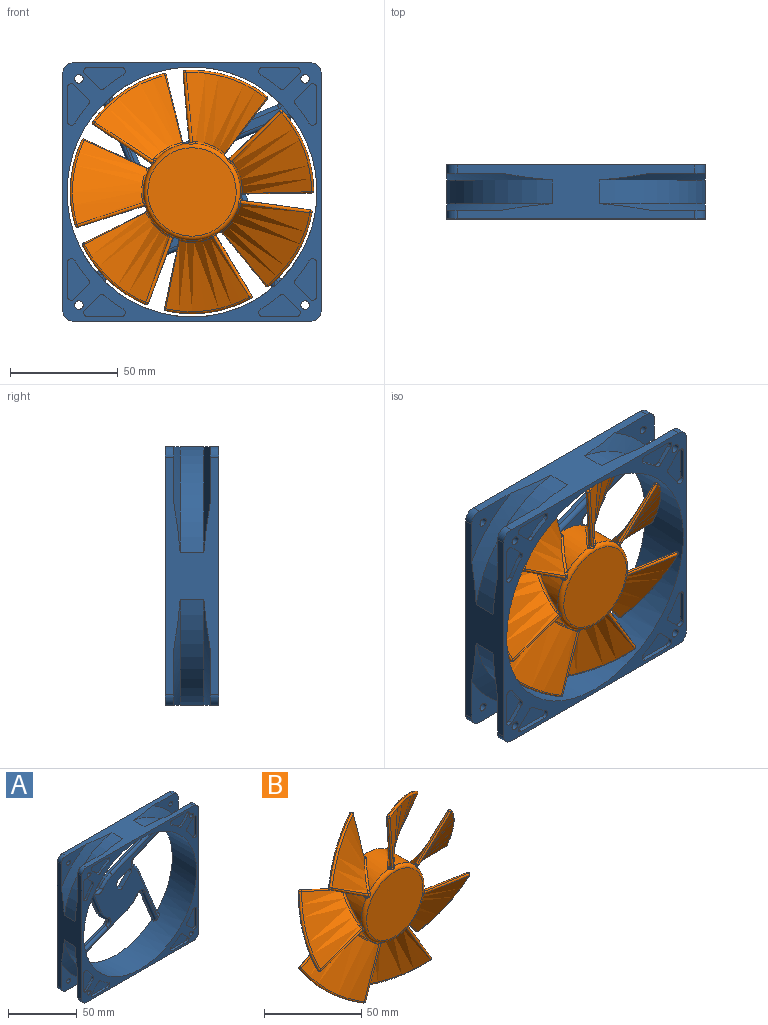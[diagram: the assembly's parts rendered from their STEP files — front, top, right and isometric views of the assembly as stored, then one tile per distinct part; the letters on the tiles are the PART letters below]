
ASSEMBLY  parts=2 mates=1
PART A: 223 faces, bbox 135.7x25x135.7 mm
  f0: plane 88.49x86.45mm, normal (0,-1,0), area 1656.3mm2, adj f15,f184,f185,f186,f187,f196,f197,f198
  f1: plane 120x120mm, normal (0,1,0), area 4802mm2, adj f2,f3,f5,f11,f12,f13,f14,f15
  f2: plane 110x25mm, normal (1,0,0), area 1352.3mm2, adj f1,f6,f23,f24,f25,f26,f27,f28
  f3: plane 6.72x2mm, normal (-1,0,0), area 13.4mm2, adj f1,f4,f35,f192
  f4: plane 65.36x42.4mm, normal (0,1,0), area 561.7mm2, adj f3,f5,f32,f33,f34,f35,f36,f182
  f5: cylinder r=2mm len=2mm, axis (0,1,0), area 1.5mm2, adj f1,f4,f32,f183
  f6: plane 120x120mm, normal (0,-1,0), area 2727.1mm2, adj f2,f7,f8,f9,f10,f12,f13,f14
  f7: cylinder r=2mm len=4mm, axis (0,1,0), area 50.3mm2, adj f6,f31
  f8: cylinder r=2mm len=4mm, axis (0,1,0), area 50.3mm2, adj f6,f26
  f9: cylinder r=2mm len=4mm, axis (0,1,0), area 50.3mm2, adj f6,f24
  f10: cylinder r=2mm len=4mm, axis (0,1,0), area 50.3mm2, adj f6,f21
  f11: plane 11.44x4mm, normal (1,0,0), area 45.8mm2, adj f1,f27,f142,f193
  f12: plane 110x25mm, normal (0,0,1), area 1413.4mm2, adj f1,f6,f26,f27,f28,f29,f30,f31
  f13: plane 110x25mm, normal (-1,0,0), area 1413.4mm2, adj f1,f6,f20,f21,f22,f29,f30,f31
  f14: plane 110x25mm, normal (0,0,-1), area 1413.4mm2, adj f1,f6,f20,f21,f22,f23,f24,f25
  f15: cylinder r=58mm len=116mm, axis (0,1,0), area 8990.7mm2, adj f0,f1,f6,f174,f175,f176,f177,f178
  f16: cylinder r=2mm len=4mm, axis (0,1,0), area 50.3mm2, adj f1,f30
  f17: cylinder r=2mm len=4mm, axis (0,1,0), area 50.3mm2, adj f1,f27
  f18: cylinder r=2mm len=4mm, axis (0,1,0), area 50.3mm2, adj f1,f23
  f19: cylinder r=2mm len=4mm, axis (0,1,0), area 50.3mm2, adj f1,f20
  f20: plane 25.93x25.93mm, normal (0,-1,0), area 257.3mm2, adj f13,f14,f19,f144,f151
  f21: plane 25.93x25.93mm, normal (0,1,0), area 257.3mm2, adj f10,f13,f14,f148,f154
  f22: cylinder r=61mm len=49mm, axis (0,1,0), area 810.7mm2, adj f13,f14,f151,f154
  f23: plane 25.93x25.93mm, normal (0,-1,0), area 257.3mm2, adj f2,f14,f18,f145,f152
  f24: plane 25.93x25.93mm, normal (0,1,0), area 257.3mm2, adj f2,f9,f14,f149,f155
  f25: cylinder r=61mm len=49mm, axis (0,1,0), area 810.7mm2, adj f2,f14,f152,f155
  f26: plane 25.93x25.93mm, normal (0,1,0), area 257.3mm2, adj f2,f8,f12,f146,f156
  f27: plane 25.93x25.93mm, normal (0,-1,0), area 240.5mm2, adj f2,f11,f12,f17,f142,f153,f191,f192
  f28: cylinder r=61mm len=49mm, axis (0,1,0), area 810.7mm2, adj f2,f12,f153,f156
  f29: cylinder r=61mm len=49mm, axis (0,1,0), area 810.7mm2, adj f12,f13,f150,f157
  f30: plane 25.93x25.93mm, normal (0,-1,0), area 257.3mm2, adj f12,f13,f16,f143,f150
  f31: plane 25.93x25.93mm, normal (0,1,0), area 257.3mm2, adj f7,f12,f13,f147,f157
  f32: plane 6.31x6.31mm, normal (0.71,0,-0.71), area 17.9mm2, adj f1,f4,f5,f36
  f33: cylinder r=63mm len=5.42mm, axis (0,1,0), area 13mm2, adj f1,f4,f35,f182
  f34: plane 4.66x2mm, normal (-1,0,0), area 9.3mm2, adj f1,f4,f36,f193
  f35: cylinder r=2mm len=3.72mm, axis (0,1,0), area 10.4mm2, adj f1,f3,f4,f33
  f36: cylinder r=2mm len=3.41mm, axis (0,-1,0), area 9.4mm2, adj f1,f4,f32,f34
  f37: plane 6.31x6.31mm, normal (-0.71,0,0.71), area 17.9mm2, adj f1,f40,f41,f43
  f38: plane 15.22x2mm, normal (0,0,-1), area 30.4mm2, adj f1,f40,f42,f43
  f39: cylinder r=63mm len=8.63mm, axis (0,1,0), area 21.2mm2, adj f1,f40,f41,f42
  f40: plane 19.22x10.31mm, normal (0,1,0), area 129.1mm2, adj f37,f38,f39,f41,f42,f43
  f41: cylinder r=2mm len=2.7mm, axis (0,1,0), area 5.9mm2, adj f1,f37,f39,f40
  f42: cylinder r=2mm len=3.72mm, axis (0,1,0), area 10.4mm2, adj f1,f38,f39,f40
  f43: cylinder r=2mm len=3.41mm, axis (0,-1,0), area 9.4mm2, adj f1,f37,f38,f40
  f44: plane 6.31x6.31mm, normal (-0.71,0,-0.71), area 17.9mm2, adj f1,f47,f48,f50
  f45: cylinder r=63mm len=8.63mm, axis (0,1,0), area 21.2mm2, adj f1,f47,f48,f49
  f46: plane 15.22x2mm, normal (0,0,1), area 30.4mm2, adj f1,f47,f49,f50
  f47: plane 19.22x10.31mm, normal (0,1,0), area 129.1mm2, adj f44,f45,f46,f48,f49,f50
  f48: cylinder r=2mm len=2.7mm, axis (0,1,0), area 5.9mm2, adj f1,f44,f45,f47
  f49: cylinder r=2mm len=3.72mm, axis (0,1,0), area 10.4mm2, adj f1,f45,f46,f47
  f50: cylinder r=2mm len=3.41mm, axis (0,-1,0), area 9.4mm2, adj f1,f44,f46,f47
  f51: plane 6.31x6.31mm, normal (-0.71,0,-0.71), area 17.9mm2, adj f1,f54,f55,f57
  f52: plane 15.22x2mm, normal (1,0,0), area 30.4mm2, adj f1,f54,f56,f57
  f53: cylinder r=63mm len=8.63mm, axis (0,1,0), area 21.2mm2, adj f1,f54,f55,f56
  f54: plane 19.22x10.31mm, normal (0,1,0), area 129.1mm2, adj f51,f52,f53,f55,f56,f57
  f55: cylinder r=2mm len=2.7mm, axis (0,1,0), area 5.9mm2, adj f1,f51,f53,f54
  f56: cylinder r=2mm len=3.72mm, axis (0,1,0), area 10.4mm2, adj f1,f52,f53,f54
  f57: cylinder r=2mm len=3.41mm, axis (0,-1,0), area 9.4mm2, adj f1,f51,f52,f54
  f58: plane 6.31x6.31mm, normal (-0.71,0,0.71), area 17.9mm2, adj f1,f61,f62,f64
  f59: cylinder r=63mm len=8.63mm, axis (0,1,0), area 21.2mm2, adj f1,f61,f62,f63
  f60: plane 15.22x2mm, normal (1,0,0), area 30.4mm2, adj f1,f61,f63,f64
  f61: plane 19.22x10.31mm, normal (0,1,0), area 129.1mm2, adj f58,f59,f60,f62,f63,f64
  f62: cylinder r=2mm len=2.7mm, axis (0,1,0), area 5.9mm2, adj f1,f58,f59,f61
  f63: cylinder r=2mm len=3.72mm, axis (0,1,0), area 10.4mm2, adj f1,f59,f60,f61
  f64: cylinder r=2mm len=3.41mm, axis (0,-1,0), area 9.4mm2, adj f1,f58,f60,f61
  f65: plane 6.31x6.31mm, normal (0.71,0,-0.71), area 17.9mm2, adj f1,f68,f69,f71
  f66: plane 15.22x2mm, normal (0,0,1), area 30.4mm2, adj f1,f68,f70,f71
  f67: cylinder r=63mm len=8.63mm, axis (0,1,0), area 21.2mm2, adj f1,f68,f69,f70
  f68: plane 19.22x10.31mm, normal (0,1,0), area 129.1mm2, adj f65,f66,f67,f69,f70,f71
  f69: cylinder r=2mm len=2.7mm, axis (0,1,0), area 5.9mm2, adj f1,f65,f67,f68
  f70: cylinder r=2mm len=3.72mm, axis (0,1,0), area 10.4mm2, adj f1,f66,f67,f68
  f71: cylinder r=2mm len=3.41mm, axis (0,-1,0), area 9.4mm2, adj f1,f65,f66,f68
  f72: plane 6.31x6.31mm, normal (0.71,0,0.71), area 17.9mm2, adj f1,f75,f76,f78
  f73: cylinder r=63mm len=8.63mm, axis (0,1,0), area 21.2mm2, adj f1,f75,f76,f77
  f74: plane 15.22x2mm, normal (0,0,-1), area 30.4mm2, adj f1,f75,f77,f78
  f75: plane 19.22x10.31mm, normal (0,1,0), area 129.1mm2, adj f72,f73,f74,f76,f77,f78
  f76: cylinder r=2mm len=2.7mm, axis (0,1,0), area 5.9mm2, adj f1,f72,f73,f75
  f77: cylinder r=2mm len=3.72mm, axis (0,1,0), area 10.4mm2, adj f1,f73,f74,f75
  f78: cylinder r=2mm len=3.41mm, axis (0,-1,0), area 9.4mm2, adj f1,f72,f74,f75
  f79: plane 6.31x6.31mm, normal (0.71,0,0.71), area 17.9mm2, adj f1,f82,f83,f85
  f80: plane 15.22x2mm, normal (-1,0,0), area 30.4mm2, adj f1,f82,f84,f85
  f81: cylinder r=63mm len=8.63mm, axis (0,1,0), area 21.2mm2, adj f1,f82,f83,f84
  f82: plane 19.22x10.31mm, normal (0,1,0), area 129.1mm2, adj f79,f80,f81,f83,f84,f85
  f83: cylinder r=2mm len=2.7mm, axis (0,1,0), area 5.9mm2, adj f1,f79,f81,f82
  f84: cylinder r=2mm len=3.72mm, axis (0,1,0), area 10.4mm2, adj f1,f80,f81,f82
  f85: cylinder r=2mm len=3.41mm, axis (0,-1,0), area 9.4mm2, adj f1,f79,f80,f82
  f86: plane 6.31x6.31mm, normal (0.71,0,-0.71), area 17.9mm2, adj f6,f89,f90,f92
  f87: plane 15.22x2mm, normal (-1,0,0), area 30.4mm2, adj f6,f89,f91,f92
  f88: cylinder r=63mm len=8.63mm, axis (0,-1,0), area 21.2mm2, adj f6,f89,f90,f91
  f89: plane 19.22x10.31mm, normal (0,-1,0), area 129.1mm2, adj f86,f87,f88,f90,f91,f92
  f90: cylinder r=2mm len=2.7mm, axis (0,-1,0), area 5.9mm2, adj f6,f86,f88,f89
  f91: cylinder r=2mm len=3.72mm, axis (0,-1,0), area 10.4mm2, adj f6,f87,f88,f89
  f92: cylinder r=2mm len=3.41mm, axis (0,1,0), area 9.4mm2, adj f6,f86,f87,f89
  f93: plane 6.31x6.31mm, normal (-0.71,0,0.71), area 17.9mm2, adj f6,f96,f97,f99
  f94: cylinder r=63mm len=8.63mm, axis (0,-1,0), area 21.2mm2, adj f6,f96,f97,f98
  f95: plane 15.22x2mm, normal (0,0,-1), area 30.4mm2, adj f6,f96,f98,f99
  f96: plane 19.22x10.31mm, normal (0,-1,0), area 129.1mm2, adj f93,f94,f95,f97,f98,f99
  f97: cylinder r=2mm len=2.7mm, axis (0,-1,0), area 5.9mm2, adj f6,f93,f94,f96
  f98: cylinder r=2mm len=3.72mm, axis (0,-1,0), area 10.4mm2, adj f6,f94,f95,f96
  f99: cylinder r=2mm len=3.41mm, axis (0,1,0), area 9.4mm2, adj f6,f93,f95,f96
  f100: plane 6.31x6.31mm, normal (-0.71,0,-0.71), area 17.9mm2, adj f6,f103,f104,f106
  f101: plane 15.22x2mm, normal (0,0,1), area 30.4mm2, adj f6,f103,f105,f106
  f102: cylinder r=63mm len=8.63mm, axis (0,-1,0), area 21.2mm2, adj f6,f103,f104,f105
  f103: plane 19.22x10.31mm, normal (0,-1,0), area 129.1mm2, adj f100,f101,f102,f104,f105,f106
  f104: cylinder r=2mm len=2.7mm, axis (0,-1,0), area 5.9mm2, adj f6,f100,f102,f103
  f105: cylinder r=2mm len=3.72mm, axis (0,-1,0), area 10.4mm2, adj f6,f101,f102,f103
  f106: cylinder r=2mm len=3.41mm, axis (0,1,0), area 9.4mm2, adj f6,f100,f101,f103
  f107: plane 6.31x6.31mm, normal (-0.71,0,-0.71), area 17.9mm2, adj f6,f110,f111,f113
  f108: cylinder r=63mm len=8.63mm, axis (0,-1,0), area 21.2mm2, adj f6,f110,f111,f112
  f109: plane 15.22x2mm, normal (1,0,0), area 30.4mm2, adj f6,f110,f112,f113
  f110: plane 19.22x10.31mm, normal (0,-1,0), area 129.1mm2, adj f107,f108,f109,f111,f112,f113
  f111: cylinder r=2mm len=2.7mm, axis (0,-1,0), area 5.9mm2, adj f6,f107,f108,f110
  f112: cylinder r=2mm len=3.72mm, axis (0,-1,0), area 10.4mm2, adj f6,f108,f109,f110
  f113: cylinder r=2mm len=3.41mm, axis (0,1,0), area 9.4mm2, adj f6,f107,f109,f110
  f114: plane 6.31x6.31mm, normal (-0.71,0,0.71), area 17.9mm2, adj f6,f117,f118,f120
  f115: plane 15.22x2mm, normal (1,0,0), area 30.4mm2, adj f6,f117,f119,f120
  f116: cylinder r=63mm len=8.63mm, axis (0,-1,0), area 21.2mm2, adj f6,f117,f118,f119
  f117: plane 19.22x10.31mm, normal (0,-1,0), area 129.1mm2, adj f114,f115,f116,f118,f119,f120
  f118: cylinder r=2mm len=2.7mm, axis (0,-1,0), area 5.9mm2, adj f6,f114,f116,f117
  f119: cylinder r=2mm len=3.72mm, axis (0,-1,0), area 10.4mm2, adj f6,f115,f116,f117
  f120: cylinder r=2mm len=3.41mm, axis (0,1,0), area 9.4mm2, adj f6,f114,f115,f117
  f121: plane 6.31x6.31mm, normal (0.71,0,-0.71), area 17.9mm2, adj f6,f124,f125,f127
  f122: cylinder r=63mm len=8.63mm, axis (0,-1,0), area 21.2mm2, adj f6,f124,f125,f126
  f123: plane 15.22x2mm, normal (0,0,1), area 30.4mm2, adj f6,f124,f126,f127
  f124: plane 19.22x10.31mm, normal (0,-1,0), area 129.1mm2, adj f121,f122,f123,f125,f126,f127
  f125: cylinder r=2mm len=2.7mm, axis (0,-1,0), area 5.9mm2, adj f6,f121,f122,f124
  f126: cylinder r=2mm len=3.72mm, axis (0,-1,0), area 10.4mm2, adj f6,f122,f123,f124
  f127: cylinder r=2mm len=3.41mm, axis (0,1,0), area 9.4mm2, adj f6,f121,f123,f124
  f128: plane 6.31x6.31mm, normal (0.71,0,0.71), area 17.9mm2, adj f6,f131,f132,f134
  f129: plane 15.22x2mm, normal (0,0,-1), area 30.4mm2, adj f6,f131,f133,f134
  f130: cylinder r=63mm len=8.63mm, axis (0,-1,0), area 21.2mm2, adj f6,f131,f132,f133
  f131: plane 19.22x10.31mm, normal (0,-1,0), area 129.1mm2, adj f128,f129,f130,f132,f133,f134
  f132: cylinder r=2mm len=2.7mm, axis (0,-1,0), area 5.9mm2, adj f6,f128,f130,f131
  f133: cylinder r=2mm len=3.72mm, axis (0,-1,0), area 10.4mm2, adj f6,f129,f130,f131
  f134: cylinder r=2mm len=3.41mm, axis (0,1,0), area 9.4mm2, adj f6,f128,f129,f131
  f135: plane 6.31x6.31mm, normal (0.71,0,0.71), area 17.9mm2, adj f6,f138,f139,f141
  f136: cylinder r=63mm len=8.63mm, axis (0,-1,0), area 21.2mm2, adj f6,f138,f139,f140
  f137: plane 15.22x2mm, normal (-1,0,0), area 30.4mm2, adj f6,f138,f140,f141
  f138: plane 19.22x10.31mm, normal (0,-1,0), area 129.1mm2, adj f135,f136,f137,f139,f140,f141
  f139: cylinder r=2mm len=2.7mm, axis (0,-1,0), area 5.9mm2, adj f6,f135,f136,f138
  f140: cylinder r=2mm len=3.72mm, axis (0,-1,0), area 10.4mm2, adj f6,f136,f137,f138
  f141: cylinder r=2mm len=3.41mm, axis (0,1,0), area 9.4mm2, adj f6,f135,f137,f138
  f142: cylinder r=5mm len=5mm, axis (0,-1,0), area 31.4mm2, adj f1,f11,f12,f27
  f143: cylinder r=5mm len=5mm, axis (0,1,0), area 31.4mm2, adj f1,f12,f13,f30
  f144: cylinder r=5mm len=5mm, axis (0,-1,0), area 31.4mm2, adj f1,f13,f14,f20
  f145: cylinder r=5mm len=5mm, axis (0,1,0), area 31.4mm2, adj f1,f2,f14,f23
  f146: cylinder r=5mm len=5mm, axis (0,-1,0), area 31.4mm2, adj f2,f6,f12,f26
  f147: cylinder r=5mm len=5mm, axis (0,1,0), area 31.4mm2, adj f6,f12,f13,f31
  f148: cylinder r=5mm len=5mm, axis (0,-1,0), area 31.4mm2, adj f6,f13,f14,f21
  f149: cylinder r=5mm len=5mm, axis (0,1,0), area 31.4mm2, adj f2,f6,f14,f24
  f150: cone r=69mm half-angle=69.4deg, axis (0,1,0), area 445.3mm2, adj f12,f13,f29,f30
  f151: cone r=69mm half-angle=69.4deg, axis (0,1,0), area 445.3mm2, adj f13,f14,f20,f22
  f152: cone r=69mm half-angle=69.4deg, axis (0,1,0), area 445.3mm2, adj f2,f14,f23,f25
  f153: cone r=69mm half-angle=69.4deg, axis (0,1,0), area 445.3mm2, adj f2,f12,f27,f28
  f154: cone r=61mm half-angle=69.4deg, axis (0,-1,0), area 445.3mm2, adj f13,f14,f21,f22
  f155: cone r=61mm half-angle=69.4deg, axis (0,-1,0), area 445.3mm2, adj f2,f14,f24,f25
  f156: cone r=61mm half-angle=69.4deg, axis (0,-1,0), area 445.3mm2, adj f2,f12,f26,f28
  f157: cone r=61mm half-angle=69.4deg, axis (0,-1,0), area 445.3mm2, adj f12,f13,f29,f31
  f158: plane 48.09x19.6mm, normal (-0.93,0,-0.38), area 103.9mm2, adj f1,f159,f174,f212
  f159: cylinder r=22.5mm len=10.34mm, axis (0,1,0), area 27.2mm2, adj f1,f158,f170,f213
  f160: plane 31.1x12.68mm, normal (-0.38,0,0.93), area 67.2mm2, adj f1,f170,f175,f215
  f161: plane 48.09x19.6mm, normal (0.38,0,-0.93), area 103.9mm2, adj f1,f162,f176,f218
  f162: cylinder r=22.5mm len=10.34mm, axis (0,1,0), area 27.2mm2, adj f1,f161,f171,f219
  f163: plane 31.1x12.68mm, normal (-0.93,0,-0.38), area 67.2mm2, adj f1,f171,f177,f221
  f164: plane 48.09x19.6mm, normal (0.93,0,0.38), area 103.9mm2, adj f1,f165,f178,f206
  f165: cylinder r=22.5mm len=8.48mm, axis (0,1,0), area 21.1mm2, adj f1,f164,f172,f207
  f166: plane 30.21x12.31mm, normal (0.38,0,-0.93), area 65.2mm2, adj f1,f172,f179,f209
  f167: plane 48.09x19.6mm, normal (-0.38,0,0.93), area 103.9mm2, adj f1,f168,f180,f200
  f168: cylinder r=22.5mm len=10.34mm, axis (0,1,0), area 27.2mm2, adj f1,f167,f173,f201
  f169: plane 31.1x12.68mm, normal (0.93,0,0.38), area 67.2mm2, adj f1,f173,f181,f203
  f170: cylinder r=3mm len=5.29mm, axis (0,1,0), area 13.1mm2, adj f1,f159,f160,f214
  f171: cylinder r=3mm len=5.29mm, axis (0,1,0), area 13.1mm2, adj f1,f162,f163,f220
  f172: cylinder r=3mm len=5.04mm, axis (0,1,0), area 12.2mm2, adj f1,f165,f166,f208
  f173: cylinder r=3mm len=5.29mm, axis (0,1,0), area 13.1mm2, adj f1,f168,f169,f202
  f174: cylinder r=1mm len=2mm, axis (0,1,0), area 4mm2, adj f1,f15,f158,f211
  f175: cylinder r=1mm len=2mm, axis (0,1,0), area 2.6mm2, adj f1,f15,f160,f216
  f176: cylinder r=1mm len=2mm, axis (0,1,0), area 4mm2, adj f1,f15,f161,f217
  f177: cylinder r=1mm len=2mm, axis (0,1,0), area 2.6mm2, adj f1,f15,f163,f222
  f178: cylinder r=1mm len=2mm, axis (0,1,0), area 4mm2, adj f1,f15,f164,f205
  f179: cylinder r=1mm len=2mm, axis (0,1,0), area 2.7mm2, adj f1,f15,f166,f210
  f180: cylinder r=1mm len=2mm, axis (0,1,0), area 4mm2, adj f1,f15,f167,f199
  f181: cylinder r=1mm len=2mm, axis (0,1,0), area 2.6mm2, adj f1,f15,f169,f204
  f182: plane 38.58x15.72mm, normal (-0.38,0,0.93), area 83.3mm2, adj f1,f4,f33,f189
  f183: plane 53.66x21.87mm, normal (0.38,0,-0.93), area 115.9mm2, adj f1,f4,f5,f190
  f184: plane 14.08x5.74mm, normal (0.93,0,0.38), area 39.7mm2, adj f0,f1,f4,f185,f190,f198
  f185: cylinder r=2.5mm len=4.09mm, axis (0,1,0), area 19.8mm2, adj f0,f1,f184,f186
  f186: plane 9.21x9.1mm, normal (-0.71,0,0.7), area 51.8mm2, adj f0,f1,f185,f187
  f187: cylinder r=2.5mm len=4mm, axis (0,1,0), area 11.2mm2, adj f0,f1,f4,f186,f188,f196
  f188: plane 3.81x2mm, normal (-0.93,0,-0.38), area 8.2mm2, adj f1,f4,f187,f189
  f189: cylinder r=2.5mm len=3.26mm, axis (0,1,0), area 7.9mm2, adj f1,f4,f182,f188
  f190: cylinder r=2.5mm len=3.26mm, axis (0,1,0), area 7.9mm2, adj f1,f4,f183,f184
  f191: cylinder r=0.5mm len=2mm, axis (0,1,0), area 1.1mm2, adj f4,f27,f192,f194
  f192: plane 4x3.21mm, normal (0,0,1), area 10.4mm2, adj f1,f2,f3,f4,f27,f191
  f193: plane 4.52x4mm, normal (0,0,-1), area 13mm2, adj f1,f4,f11,f27,f34,f195
  f194: plane 2.83x2mm, normal (0.91,0,0.42), area 6.2mm2, adj f4,f27,f191,f195
  f195: cylinder r=0.5mm len=2mm, axis (0,1,0), area 2mm2, adj f4,f27,f193,f194
  f196: cylinder r=2.5mm len=3.17mm, axis (0,1,0), area 7.4mm2, adj f0,f4,f187,f197
  f197: plane 11.02x4.49mm, normal (0.38,0,-0.93), area 23.8mm2, adj f0,f4,f196,f198
  f198: cylinder r=2.5mm len=3.26mm, axis (0,1,0), area 7.9mm2, adj f0,f4,f184,f197
  f199: torus R=3mm, axis (0,-1,0), area 5.8mm2, adj f0,f15,f180,f200
  f200: cylinder r=2mm len=48.84mm, axis (0.93,0,0.38), area 163.1mm2, adj f0,f167,f199,f201
  f201: torus R=20.5mm, axis (0,-1,0), area 41.4mm2, adj f0,f168,f200,f202
  f202: torus R=5mm, axis (0,-1,0), area 25.5mm2, adj f0,f173,f201,f203
  f203: cylinder r=2mm len=31.85mm, axis (0.38,0,-0.93), area 105.5mm2, adj f0,f169,f202,f204
  f204: torus R=3mm, axis (0,-1,0), area 1.9mm2, adj f0,f15,f181,f203
  f205: torus R=3mm, axis (0,-1,0), area 5.8mm2, adj f0,f15,f178,f206
  f206: cylinder r=2mm len=48.84mm, axis (0.38,0,-0.93), area 163.1mm2, adj f0,f164,f205,f207
  f207: torus R=20.5mm, axis (0,-1,0), area 32mm2, adj f0,f165,f206,f208
  f208: torus R=5mm, axis (0,-1,0), area 23.9mm2, adj f0,f172,f207,f209
  f209: cylinder r=2mm len=30.96mm, axis (-0.93,0,-0.38), area 102.5mm2, adj f0,f166,f208,f210
  f210: torus R=3mm, axis (0,-1,0), area 2.2mm2, adj f0,f15,f179,f209
  f211: torus R=3mm, axis (0,-1,0), area 5.8mm2, adj f0,f15,f174,f212
  f212: cylinder r=2mm len=48.84mm, axis (-0.38,0,0.93), area 163.1mm2, adj f0,f158,f211,f213
  f213: torus R=20.5mm, axis (0,-1,0), area 41.4mm2, adj f0,f159,f212,f214
  f214: torus R=5mm, axis (0,-1,0), area 25.5mm2, adj f0,f170,f213,f215
  f215: cylinder r=2mm len=31.85mm, axis (0.93,0,0.38), area 105.5mm2, adj f0,f160,f214,f216
  f216: torus R=3mm, axis (0,-1,0), area 1.9mm2, adj f0,f15,f175,f215
  f217: torus R=3mm, axis (0,-1,0), area 5.8mm2, adj f0,f15,f176,f218
  f218: cylinder r=2mm len=48.84mm, axis (-0.93,0,-0.38), area 163.1mm2, adj f0,f161,f217,f219
  f219: torus R=20.5mm, axis (0,-1,0), area 41.4mm2, adj f0,f162,f218,f220
  f220: torus R=5mm, axis (0,-1,0), area 25.5mm2, adj f0,f171,f219,f221
  f221: cylinder r=2mm len=31.85mm, axis (-0.38,0,0.93), area 105.5mm2, adj f0,f163,f220,f222
  f222: torus R=3mm, axis (0,-1,0), area 1.9mm2, adj f0,f15,f177,f221
PART B: 143 faces, bbox 115.5x27x115.7 mm
  f0: cylinder r=22.5mm len=28.95mm, axis (0,1,0), area 269.8mm2, adj f8,f72,f79,f81,f82,f133,f134
  f1: cylinder r=22.5mm len=25.02mm, axis (0,1,0), area 269.8mm2, adj f8,f72,f73,f74,f89,f91,f92
  f2: cylinder r=22.5mm len=27.37mm, axis (0,1,0), area 269.8mm2, adj f8,f72,f83,f84,f99,f101,f102
  f3: cylinder r=22.5mm len=27.74mm, axis (0,1,0), area 269.8mm2, adj f8,f72,f93,f94,f109,f111,f112
  f4: cylinder r=22.5mm len=24.42mm, axis (0,1,0), area 269.8mm2, adj f8,f72,f103,f104,f119,f121,f122
  f5: cylinder r=22.5mm len=29.07mm, axis (0,1,0), area 269.8mm2, adj f8,f72,f113,f114,f129,f131,f132
  f6: cylinder r=22.5mm len=21.04mm, axis (0,1,0), area 269.8mm2, adj f8,f72,f123,f124,f139,f141,f142
  f7: plane 41x41mm, normal (0,-1,0), area 1320.3mm2, adj f72
  f8: plane 45.12x45.12mm, normal (0,1,0), area 1590.4mm2, adj f0,f1,f2,f3,f4,f5,f6,f75
  f9: bspline ~48.93x45.75mm, area 1052.8mm2, adj f10,f12,f15,f141
  f10: bspline ~27.23x25.53mm, area 50.4mm2, adj f9,f11,f14,f140,f142
  f11: bspline ~24.34x23.49mm, area 50.8mm2, adj f10,f14,f138
  f12: bspline ~36.29x1.66mm, area 50.5mm2, adj f9,f13,f17,f137,f139
  f13: bspline ~36.94x1.66mm, area 50.4mm2, adj f12,f17,f133,f135
  f14: sphere r=1mm, area 3.8mm2, adj f10,f11,f15,f16
  f15: bspline ~39.27x19.01mm, area 69.1mm2, adj f9,f14,f16,f17
  f16: bspline ~39.38x19.01mm, area 69.1mm2, adj f14,f15,f17
  f17: sphere r=1mm, area 2.8mm2, adj f12,f13,f15,f16
  f18: bspline ~55.87x39.92mm, area 1052.8mm2, adj f19,f21,f24,f131
  f19: bspline ~36.44x3.68mm, area 50.4mm2, adj f18,f20,f23,f130,f132
  f20: bspline ~32.44x4.35mm, area 50.8mm2, adj f19,f23,f128
  f21: bspline ~29.36x23.45mm, area 50.5mm2, adj f18,f22,f26,f127,f129
  f22: bspline ~29.89x23.03mm, area 50.4mm2, adj f21,f26,f123,f125
  f23: sphere r=1mm, area 3.8mm2, adj f19,f20,f24,f25
  f24: bspline ~40.3x19.01mm, area 69.1mm2, adj f18,f23,f25,f26
  f25: bspline ~40.22x19.01mm, area 69.1mm2, adj f23,f24,f26
  f26: sphere r=1mm, area 2.8mm2, adj f21,f22,f24,f25
  f27: bspline ~49.21x48.75mm, area 1052.8mm2, adj f28,f30,f33,f121
  f28: bspline ~30.69x21.14mm, area 50.4mm2, adj f27,f29,f32,f120,f122
  f29: bspline ~27.9x18.94mm, area 50.8mm2, adj f28,f32,f118
  f30: bspline ~35.62x9.68mm, area 50.5mm2, adj f27,f31,f35,f117,f119
  f31: bspline ~36.01x9.83mm, area 50.4mm2, adj f30,f35,f113,f115
  f32: sphere r=1mm, area 3.8mm2, adj f28,f29,f33,f34
  f33: bspline ~34.86x24.31mm, area 69.1mm2, adj f27,f32,f34,f35
  f34: bspline ~35.24x23.75mm, area 69.1mm2, adj f32,f33,f35
  f35: sphere r=1mm, area 2.8mm2, adj f30,f31,f33,f34
  f36: bspline ~56.34x39.45mm, area 1052.8mm2, adj f37,f39,f42,f111
  f37: bspline ~35.08x11.67mm, area 50.4mm2, adj f36,f38,f41,f110,f112
  f38: bspline ~31.26x11.41mm, area 50.8mm2, adj f37,f41,f108
  f39: bspline ~33.37x16.7mm, area 50.5mm2, adj f36,f40,f44,f107,f109
  f40: bspline ~33.97x16.03mm, area 50.4mm2, adj f39,f44,f103,f105
  f41: sphere r=1mm, area 3.8mm2, adj f37,f38,f42,f43
  f42: bspline ~42.06x19.01mm, area 69.1mm2, adj f36,f41,f43,f44
  f43: bspline ~39.86x18.13mm, area 69.1mm2, adj f41,f42,f44
  f44: sphere r=1mm, area 2.8mm2, adj f39,f40,f42,f43
  f45: bspline ~49.3x47.01mm, area 1052.8mm2, adj f46,f48,f51,f101
  f46: bspline ~34.32x13.99mm, area 50.4mm2, adj f45,f47,f50,f100,f102
  f47: bspline ~30.91x12.6mm, area 50.8mm2, adj f46,f50,f98
  f48: bspline ~33.16x17.22mm, area 50.5mm2, adj f45,f49,f53,f97,f99
  f49: bspline ~33.28x17.51mm, area 50.4mm2, adj f48,f53,f93,f95
  f50: sphere r=1mm, area 3.8mm2, adj f46,f47,f51,f52
  f51: bspline ~31.27x28.78mm, area 69.1mm2, adj f45,f50,f52,f53
  f52: bspline ~30.72x29.34mm, area 69.1mm2, adj f50,f51,f53
  f53: sphere r=1mm, area 2.8mm2, adj f48,f49,f51,f52
  f54: bspline ~53.99x42.68mm, area 1052.8mm2, adj f55,f57,f60,f91
  f55: bspline ~31.95x19.08mm, area 50.4mm2, adj f54,f56,f59,f90,f92
  f56: bspline ~28.51x17.9mm, area 50.8mm2, adj f55,f59,f88
  f57: bspline ~35.69x9.11mm, area 50.5mm2, adj f54,f58,f62,f87,f89
  f58: bspline ~36.35x8.23mm, area 50.4mm2, adj f57,f62,f83,f85
  f59: sphere r=1mm, area 3.8mm2, adj f55,f56,f60,f61
  f60: bspline ~41.72x19.01mm, area 69.1mm2, adj f54,f59,f61,f62
  f61: bspline ~39.66x18.13mm, area 69.1mm2, adj f59,f60,f62
  f62: sphere r=1mm, area 2.8mm2, adj f57,f58,f60,f61
  f63: bspline ~52.59x43.95mm, area 1052.8mm2, adj f64,f66,f69,f81
  f64: bspline ~36.23x6.14mm, area 50.4mm2, adj f63,f65,f68,f80,f82
  f65: bspline ~32.38x5.62mm, area 50.8mm2, adj f64,f68,f78
  f66: bspline ~29.03x23.89mm, area 50.5mm2, adj f63,f67,f71,f77,f79
  f67: bspline ~28.88x24.31mm, area 50.4mm2, adj f66,f71,f73,f75
  f68: sphere r=1mm, area 3.8mm2, adj f64,f65,f69,f70
  f69: bspline ~36.67x21.42mm, area 69.1mm2, adj f63,f68,f70,f71
  f70: bspline ~36.38x21.97mm, area 69.1mm2, adj f68,f69,f71
  f71: sphere r=1mm, area 2.8mm2, adj f66,f67,f69,f70
  f72: torus R=20.5mm, axis (0,-1,0), area 399.1mm2, adj f0,f1,f2,f3,f4,f5,f6,f7
  f73: bspline ~3.19x1.73mm, area 3.2mm2, adj f1,f67,f74,f75
  f74: bspline ~18.77x14.22mm, area 31.6mm2, adj f1,f73,f76
  f75: bspline ~1.25x0.84mm, area 0mm2, adj f8,f67,f73,f77
  f76: bspline ~2.92x2.67mm, area 2.3mm2, adj f72,f74,f78
  f77: bspline ~2.41x2.19mm, area 2.1mm2, adj f8,f66,f75,f79
  f78: bspline ~3.17x1.53mm, area 2.2mm2, adj f65,f72,f76,f80
  f79: bspline ~1.5x1.16mm, area 0mm2, adj f0,f66,f77,f81
  f80: bspline ~1.52x1.39mm, area 1.2mm2, adj f64,f72,f78,f82
  f81: bspline ~23.03x19.48mm, area 35.5mm2, adj f0,f63,f79,f82
  f82: bspline ~2.15x1.56mm, area 1.7mm2, adj f0,f64,f80,f81
  f83: bspline ~3.19x1.35mm, area 3.2mm2, adj f2,f58,f84,f85
  f84: bspline ~18.77x17.65mm, area 31.6mm2, adj f2,f83,f86
  f85: bspline ~1.13x0.73mm, area 0mm2, adj f8,f58,f83,f87
  f86: bspline ~3.03x2.67mm, area 2.3mm2, adj f72,f84,f88
  f87: bspline ~2.64x1.45mm, area 2.1mm2, adj f8,f57,f85,f89
  f88: bspline ~2.88x1.93mm, area 2.2mm2, adj f56,f72,f86,f90
  f89: bspline ~1.3x1.16mm, area 0mm2, adj f1,f57,f87,f91
  f90: bspline ~1.39x1.36mm, area 1.2mm2, adj f55,f72,f88,f92
  f91: bspline ~21.59x19.42mm, area 35.5mm2, adj f1,f54,f89,f92
  f92: bspline ~2.15x1.57mm, area 1.7mm2, adj f1,f55,f90,f91
  f93: bspline ~3.19x1.7mm, area 3.2mm2, adj f3,f49,f94,f95
  f94: bspline ~18.77x14.05mm, area 31.6mm2, adj f3,f93,f96
  f95: bspline ~1.16x0.96mm, area 0mm2, adj f8,f49,f93,f97
  f96: bspline ~2.67x2.6mm, area 2.3mm2, adj f72,f94,f98
  f97: bspline ~2.71x1.87mm, area 2.1mm2, adj f8,f48,f95,f99
  f98: bspline ~2.95x1.93mm, area 2.2mm2, adj f47,f72,f96,f100
  f99: bspline ~1.42x1.16mm, area 0mm2, adj f2,f48,f97,f101
  f100: bspline ~1.55x1.39mm, area 1.2mm2, adj f46,f72,f98,f102
  f101: bspline ~23.03x17.03mm, area 35.5mm2, adj f2,f45,f99,f102
  f102: bspline ~1.95x1.57mm, area 1.7mm2, adj f2,f46,f100,f101
  f103: bspline ~3.19x1.54mm, area 3.2mm2, adj f4,f40,f104,f105
  f104: bspline ~18.77x17.12mm, area 31.6mm2, adj f4,f103,f106
  f105: bspline ~1.23x0.75mm, area 0mm2, adj f8,f40,f103,f107
  f106: bspline ~3.15x2.67mm, area 2.3mm2, adj f72,f104,f108
  f107: bspline ~2.71x1.89mm, area 2.1mm2, adj f8,f39,f105,f109
  f108: bspline ~3.14x1.5mm, area 2.2mm2, adj f38,f72,f106,f110
  f109: bspline ~1.44x1.16mm, area 0mm2, adj f3,f39,f107,f111
  f110: bspline ~1.39x1.29mm, area 1.2mm2, adj f37,f72,f108,f112
  f111: bspline ~23.03x21.38mm, area 35.5mm2, adj f3,f36,f109,f112
  f112: bspline ~2.15x1.37mm, area 1.7mm2, adj f3,f37,f110,f111
  f113: bspline ~3.19x1.58mm, area 3.2mm2, adj f5,f31,f114,f115
  f114: bspline ~18.77x16.07mm, area 31.6mm2, adj f5,f113,f116
  f115: bspline ~1.01x0.99mm, area 0mm2, adj f8,f31,f113,f117
  f116: bspline ~2.67x2.41mm, area 2.3mm2, adj f72,f114,f118
  f117: bspline ~2.94x1.46mm, area 2.1mm2, adj f8,f30,f115,f119
  f118: bspline ~2.58x2.29mm, area 2.2mm2, adj f29,f72,f116,f120
  f119: bspline ~1.27x1.16mm, area 0mm2, adj f4,f30,f117,f121
  f120: bspline ~1.5x1.39mm, area 1.2mm2, adj f28,f72,f118,f122
  f121: bspline ~23.03x17.18mm, area 35.5mm2, adj f4,f27,f119,f122
  f122: bspline ~1.95x1.63mm, area 1.7mm2, adj f4,f28,f120,f121
  f123: bspline ~3.19x1.68mm, area 3.2mm2, adj f6,f22,f124,f125
  f124: bspline ~18.77x15.94mm, area 31.6mm2, adj f6,f123,f126
  f125: bspline ~1.17x0.71mm, area 0mm2, adj f8,f22,f123,f127
  f126: bspline ~3.11x2.67mm, area 2.3mm2, adj f72,f124,f128
  f127: bspline ~2.22x2.08mm, area 2.1mm2, adj f8,f21,f125,f129
  f128: bspline ~3.24x1.28mm, area 2.2mm2, adj f20,f72,f126,f130
  f129: bspline ~1.51x1.16mm, area 0mm2, adj f5,f21,f127,f131
  f130: bspline ~1.41x1.39mm, area 1.2mm2, adj f19,f72,f128,f132
  f131: bspline ~23.03x20.96mm, area 35.5mm2, adj f5,f18,f129,f132
  f132: bspline ~2.15x1.41mm, area 1.7mm2, adj f5,f19,f130,f131
  f133: bspline ~3.19x1.4mm, area 3.2mm2, adj f0,f13,f134,f135
  f134: bspline ~18.77x17.3mm, area 31.6mm2, adj f0,f133,f136
  f135: bspline ~1.05x0.82mm, area 0mm2, adj f8,f13,f133,f137
  f136: bspline ~2.64x2.41mm, area 2.3mm2, adj f72,f134,f138
  f137: bspline ~3.01x1.1mm, area 2.1mm2, adj f8,f12,f135,f139
  f138: bspline ~2.53x2.27mm, area 2.2mm2, adj f11,f72,f136,f140
  f139: bspline ~1.16x1.13mm, area 0mm2, adj f6,f12,f137,f141
  f140: bspline ~1.4x1.39mm, area 1.2mm2, adj f10,f72,f138,f142
  f141: bspline ~23.03x19.39mm, area 35.5mm2, adj f6,f9,f139,f142
  f142: bspline ~2.15x1.7mm, area 1.7mm2, adj f6,f10,f140,f141
PLACE A at identity fixed
PLACE B at identity
MATE revolute A.f15 <-> B.f0  axis (0,-1,0) through (0,-25,0)mm
